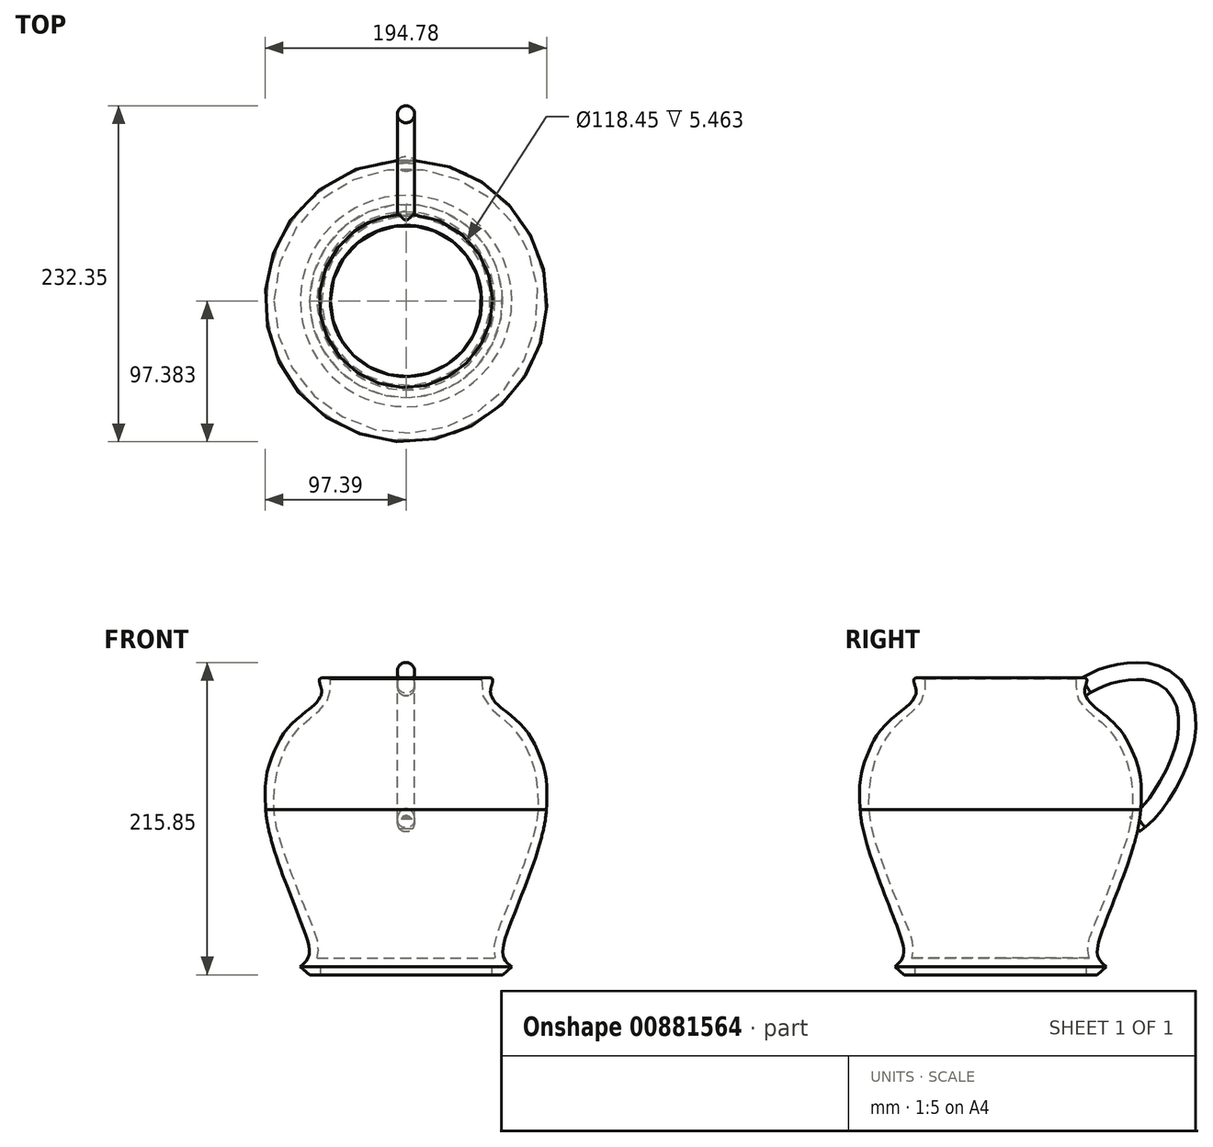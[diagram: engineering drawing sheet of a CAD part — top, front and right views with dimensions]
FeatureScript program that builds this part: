
annotation { "Feature Type Name" : "Feature", "Feature Type Description" : "" }
export const myFeature = defineFeature(function(context is Context, id is Id, definition is map)
    precondition{}
    {
        {
            var Q0;
            Q0=qCreatedBy(makeId("Right.planeOp"),FACE);
            var sketch = newSketch(context, id + "F0", { "sketchPlane" : qUnion([Q0])});
            skLineSegment(sketch, "E0", {"start": v(21, -90.01) * mm, "end": v(21, 114.99) * mm});
            skLineSegment(sketch, "E1", {"start": v(21, -78.5) * mm, "end": v(82.52, -78.5) * mm});
            skLineSegment(sketch, "E2", {"start": v(21, -84.55) * mm, "end": v(80.23, -84.55) * mm});
            skLineSegment(sketch, "E3", {"start": v(80.23, -84.55) * mm, "end": v(80.23, -90.01) * mm});
            skLineSegment(sketch, "E4", {"start": v(80.23, -90.01) * mm, "end": v(87.7, -90.01) * mm});
            skLineSegment(sketch, "E5", {"start": v(87.7, -90.01) * mm, "end": v(94.08, -84.43) * mm});
            skFitSpline(sketch, "E6", {"points": [v(82.52, -78.5) * mm, v(81.64, -74.25) * mm, v(81.95, -67.69) * mm, v(84.48, -59.55) * mm, v(88.62, -49.21) * mm, v(95.1, -33.23) * mm, v(101.8, -15.16) * mm, v(108.67, 4.78) * mm, v(111.86, 19.84) * mm, v(112.27, 30.65) * mm, v(111.12, 44.97) * mm, v(107.42, 59.27) * mm, v(101.35, 71.94) * mm, v(94.22, 81.28) * mm, v(85.7, 88.72) * mm, v(77.6, 96.36) * mm, v(73.85, 103.6) * mm, v(73.28, 114.6) * mm], "startDerivative": vector(-29.85, 113.51) * mm, "endDerivative": vector(3.8, 206.97) * mm});
            skFitSpline(sketch, "E7", {"points": [v(94.08, -84.43) * mm, v(89.53, -79.86) * mm, v(87.84, -73.83) * mm, v(90.13, -63.11) * mm, v(96.16, -47.09) * mm, v(102.34, -31.05) * mm, v(107.8, -16.74) * mm, v(113.24, 0) * mm, v(117.16, 16.62) * mm, v(118.13, 27.14) * mm, v(118.26, 40.74) * mm, v(115.83, 54.5) * mm, v(109.82, 69.46) * mm, v(103.55, 79.43) * mm, v(92.49, 90.01) * mm, v(84.6, 96.46) * mm, v(80.19, 102.2) * mm, v(79.6, 107.78) * mm, v(80.6, 114.6) * mm, v(73.28, 114.6) * mm, v(69.42, 114.6) * mm, v(69.28, 114.6) * mm], "startDerivative": vector(-134.88, 112.2) * mm, "endDerivative": vector(-18, -1) * mm});
            skFitSpline(sketch, "E8", {"points": [v(113.24, 0) * mm, v(118.25, 6.85) * mm, v(127.82, 18.08) * mm, v(140.2, 35.32) * mm, v(151.18, 56.76) * mm, v(154.55, 66.35) * mm, v(156.68, 76.37) * mm, v(156.98, 90.03) * mm, v(152.29, 105.83) * mm, v(137.56, 119.41) * mm, v(117.06, 123.43) * mm, v(98.48, 120.95) * mm, v(80.6, 114.6) * mm], "startDerivative": vector(74.69, 108.6) * mm, "endDerivative": vector(-180.14, -73.73) * mm});
            skFitSpline(sketch, "E9", {"points": [v(80.19, 102.2) * mm, v(80.19, 105.26) * mm, v(88.07, 110.54) * mm, v(95.23, 113.65) * mm, v(107.27, 116.35) * mm, v(118.5, 115.81) * mm, v(129.04, 111.21) * mm, v(136.75, 103.64) * mm, v(141.49, 93.5) * mm, v(142.76, 78.66) * mm, v(140.62, 67.61) * mm, v(137.79, 58.5) * mm, v(132.62, 47.14) * mm, v(126.04, 36.4) * mm, v(120.87, 28.6) * mm, v(117.97, 24.12) * mm, v(117.97, 24.07) * mm], "startDerivative": vector(-36.79, 139.84) * mm, "endDerivative": vector(2.08, -6.5) * mm});
            skSolve(sketch);
        }
        {
            var Q0;
            {var subQ9=sQuery(id+"F0.wireOp",EDGE,"E1");Q0=makeQuery(id+"F0.imprint","IMPRINT",FACE,{"disambiguationData":[TD([[makeQuery(id+"F0.imprint","IMPRINT",EDGE,{"derivedFrom":subQ9}),-1.0]])]});}
            var Q1;
            Q1=sQuery(id+"F0.wireOp",EDGE,"E0");
            revolve(context, id + "F1", {"surfaceOperationType" : NewSurfaceOperationType.NEW, "entities" : qUnion([Q0]), "axis" : qUnion([Q1]), "revolveType" : RevolveType.FULL});
        }
        {
            var Q0;
            {var subQ0=sQuery(id+"F0.wireOp",EDGE,"E8");Q0=makeQuery(id+"F0.imprint","IMPRINT",FACE,{"disambiguationData":[TD([[makeQuery(id+"F0.imprint","IMPRINT",EDGE,{"derivedFrom":subQ0}),1.0]])]});}
            var sketch = newSketch(context, id + "F2", { "sketchPlane" : qUnion([Q0])});
            skFitSpline(sketch, "E10", {"points": [v(80.22, 110.04) * mm, v(86.02, 113.07) * mm, v(95.25, 116.76) * mm, v(104.74, 118.94) * mm, v(113.77, 119.8) * mm, v(125.39, 118.87) * mm, v(138.6, 112.2) * mm, v(146.59, 101.32) * mm, v(149.64, 90.1) * mm, v(149.67, 77.28) * mm, v(147.25, 65.34) * mm, v(139.8, 47.05) * mm, v(133.3, 35.87) * mm, v(124.35, 23.27) * mm, v(117.15, 16.62) * mm], "startDerivative": vector(102.22, 56.16) * mm, "endDerivative": vector(-111.6, -93.54) * mm});
            skLineSegment(sketch, "E11", {"start": v(80.22, 110.04) * mm, "end": v(77.08, 108.07) * mm});
            skLineSegment(sketch, "E12", {"start": v(117.15, 16.62) * mm, "end": v(113.82, 14.08) * mm});
            skSolve(sketch);
        }
        {
            var Q0;
            Q0=sQuery(id+"F2.wireOp",VERTEX,"E10.start");
            var Q1;
            Q1=sQuery(id+"F2.wireOp",EDGE,"E10");
            cPlane(context, id + "F3", {"entities" : qUnion([Q0, Q1]), "cplaneType" : CPlaneType.CURVE_POINT, "offset" : 25 * mm, "width" : 150 * mm, "height" : 150 * mm});
        }
        {
            var Q0;
            Q0=qCreatedBy(id+"F3.planeOp",FACE);
            var sketch = newSketch(context, id + "F4", { "sketchPlane" : qUnion([Q0])});
            skCircle(sketch, "E13", {"center": v(0, 57.88) * mm, "radius": 5.93 * mm});
            skSolve(sketch);
        }
        {
            var Q0;
            Q0=makeQuery(id+"F4.imprint","IMPRINT",FACE,{"disambiguationData":[TD([[makeQuery(id+"F4.imprint","IMPRINT",EDGE,{"derivedFrom":sQuery(id+"F4.wireOp",EDGE,"E13")}),1.0]])]});
            var Q1;
            Q1=sQuery(id+"F2.wireOp",EDGE,"E10");
            var Q2;
            Q2=sQuery(id+"F2.wireOp",EDGE,"E11");
            var Q3;
            Q3=sQuery(id+"F2.wireOp",EDGE,"E12");
            sweep(context, id + "F5", {"operationType" : NewBodyOperationType.ADD, "profiles" : qUnion([Q0]), "path" : qUnion([Q1, Q2, Q3])});
        }
    });
